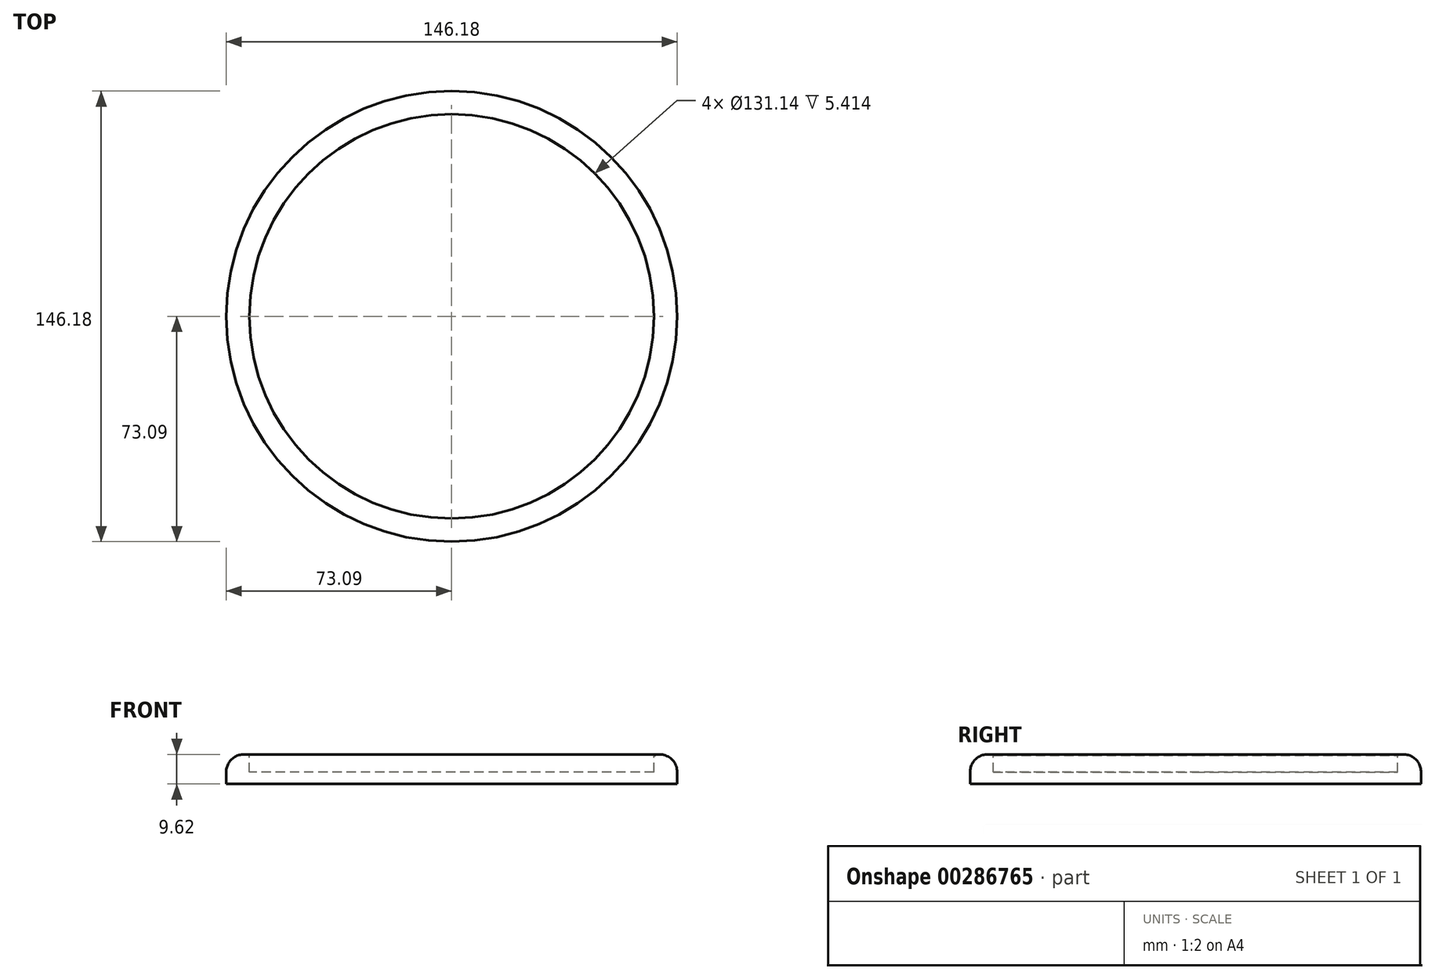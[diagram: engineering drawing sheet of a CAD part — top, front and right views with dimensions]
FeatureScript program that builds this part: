
annotation { "Feature Type Name" : "Feature", "Feature Type Description" : "" }
export const myFeature = defineFeature(function(context is Context, id is Id, definition is map)
    precondition{}
    {
        {
            var Q0;
            Q0=qCreatedBy(makeId("Front.planeOp"),FACE);
            var sketch = newSketch(context, id + "F0", { "sketchPlane" : qUnion([Q0])});
            skLineSegment(sketch, "E0", {"start": v(0, 0) * mm, "end": v(73.1, 0) * mm});
            skLineSegment(sketch, "E1", {"start": v(73.1, 0) * mm, "end": v(73.1, 3.91) * mm});
            skArc(sketch, "E2", {"start": v(73.1, 3.91) * mm, "mid": v(70.72, 8.54) * mm, "end": v(65.57, 9.32) * mm});
            skLineSegment(sketch, "E3", {"start": v(65.57, 9.32) * mm, "end": v(65.57, 3.91) * mm});
            skLineSegment(sketch, "E4", {"start": v(65.57, 3.91) * mm, "end": v(0, 3.91) * mm});
            skLineSegment(sketch, "E5", {"start": v(0, 3.91) * mm, "end": v(0, 0) * mm});
            skSolve(sketch);
        }
        {
            var Q0;
            Q0=makeQuery(id+"F0.imprint","IMPRINT",FACE,{"disambiguationData":[TD([[makeQuery(id+"F0.imprint","IMPRINT",EDGE,{"derivedFrom":sQuery(id+"F0.wireOp",EDGE,"E0")}),1.0]])]});
            var Q1;
            Q1=sQuery(id+"F0.wireOp",EDGE,"E5");
            revolve(context, id + "F1", {"entities" : qUnion([Q0]), "axis" : qUnion([Q1]), "revolveType" : RevolveType.FULL});
        }
    });
